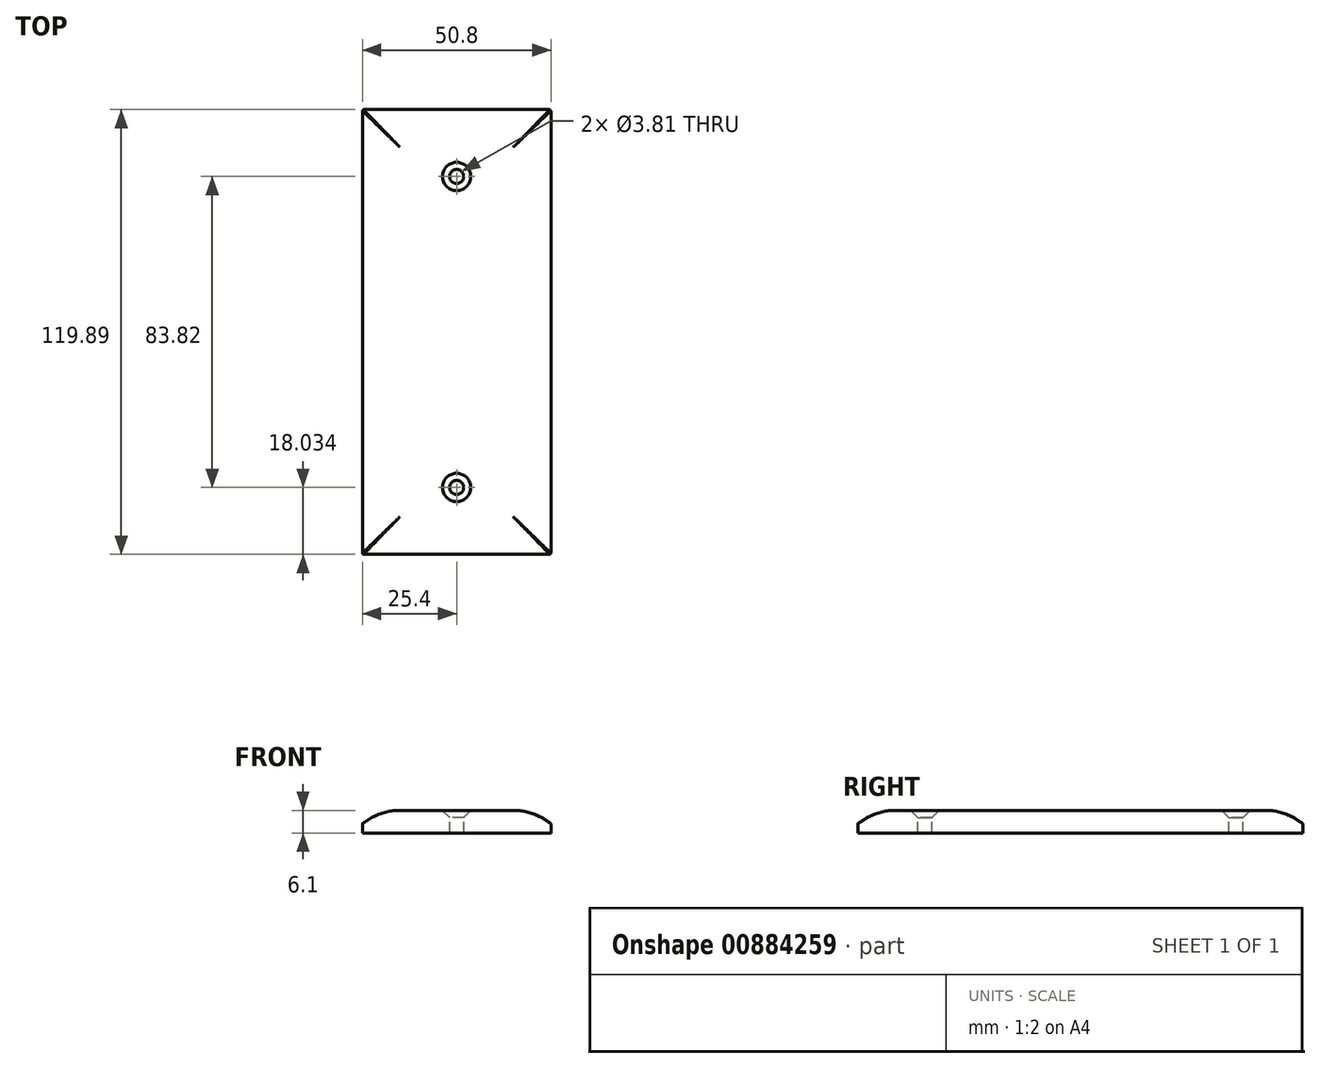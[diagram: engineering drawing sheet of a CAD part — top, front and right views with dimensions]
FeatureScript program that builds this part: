
annotation { "Feature Type Name" : "Feature", "Feature Type Description" : "" }
export const myFeature = defineFeature(function(context is Context, id is Id, definition is map)
    precondition{}
    {
        {
            var Q0;
            Q0=qCreatedBy(makeId("Top.planeOp"),FACE);
            var sketch = newSketch(context, id + "F0", { "sketchPlane" : qUnion([Q0])});
            skLineSegment(sketch, "E0.bottom", {"start": v(0, 0) * mm, "end": v(50.8, 0) * mm});
            skLineSegment(sketch, "E0.top", {"start": v(0, 119.89) * mm, "end": v(50.8, 119.89) * mm});
            skLineSegment(sketch, "E0.left", {"start": v(0, 0) * mm, "end": v(0, 119.89) * mm});
            skLineSegment(sketch, "E0.right", {"start": v(50.8, 0) * mm, "end": v(50.8, 119.89) * mm});
            skSolve(sketch);
        }
        {
            var Q0;
            Q0 = qSketchRegion(id + "F0", true);
            extrude(context, id + "F1", {"entities" : qUnion([Q0]), "depth" : 6.1 * mm, "offsetDistance" : 25.4 * mm});
        }
        {
            var Q0;
            Q0=makeQuery(id+"F1.opExtrude","CAP_FACE",FACE,{"disambiguationData":[OSD([sQuery(id+"F0.wireOp",EDGE,"E0.bottom"),sQuery(id+"F0.wireOp",EDGE,"E0.top"),sQuery(id+"F0.wireOp",EDGE,"E0.left"),sQuery(id+"F0.wireOp",EDGE,"E0.right")])],"isStart":false});
            var sketch = newSketch(context, id + "F2", { "sketchPlane" : qUnion([Q0])});
            skLineSegment(sketch, "E1", {"start": v(25.4, 0) * mm, "end": v(25.4, 119.89) * mm, "construction": true});
            skPoint(sketch, "E2", {"position": v(25.4, 18.03) * mm});
            skPoint(sketch, "E3", {"position": v(25.4, 101.85) * mm});
            skLineSegment(sketch, "E4", {"start": v(0, 59.94) * mm, "end": v(50.8, 59.94) * mm, "construction": true});
            skPoint(sketch, "E5", {"position": v(50.8, 59.94) * mm});
            skSolve(sketch);
        }
        {
            var Q0;
            Q0=sQuery(id+"F2.wireOp",VERTEX,"E3");
            var Q1;
            Q1=sQuery(id+"F2.wireOp",VERTEX,"E2");
            var Q2;
            Q2=makeQuery(id+"F1.opExtrude","SWEPT_BODY",BODY,{"disambiguationData":[OSD([sQuery(id+"F0.wireOp",EDGE,"E0.bottom"),sQuery(id+"F0.wireOp",EDGE,"E0.top"),sQuery(id+"F0.wireOp",EDGE,"E0.left"),sQuery(id+"F0.wireOp",EDGE,"E0.right")])]});
            hole(context, id + "F3", {"style" : HoleStyle.C_SINK, "endStyle" : HoleEndStyle.THROUGH, "holeDiameter" : 3.8 * mm, "cSinkDiameter" : 7.62 * mm, "cSinkAngle" : 90 * degree, "majorDiameter" : 6.35 * mm, "isTappedThrough" : true, "tappedDepth" : 12.7 * mm, "tapClearance" : 3, "locations" : qUnion([Q0, Q1]), "scope" : qUnion([Q2])});
        }
        {
            var Q0;
            Q0=makeQuery(id+"F1.opExtrude","SWEPT_FACE",FACE,{"disambiguationData":[OSD([sQuery(id+"F0.wireOp",EDGE,"E0.bottom")])]});
            var sketch = newSketch(context, id + "F4", { "sketchPlane" : qUnion([Q0])});
            skArc(sketch, "E6", {"start": v(0.2, 2.7) * mm, "mid": v(4.9, 5.22) * mm, "end": v(10.16, 6.1) * mm});
            skLineSegment(sketch, "E7", {"start": v(25.4, 0) * mm, "end": v(25.4, 6.1) * mm, "construction": true});
            skPoint(sketch, "E8.visualSharp", {"position": v(0, 2.54) * mm});
            skLineSegment(sketch, "E9", {"start": v(10.16, 6.1) * mm, "end": v(0, 6.1) * mm});
            skLineSegment(sketch, "E10", {"start": v(0, 6.1) * mm, "end": v(0, 2.54) * mm});
            skLineSegment(sketch, "E11", {"start": v(10.16, 6.1) * mm, "end": v(25.4, 6.1) * mm, "construction": true});
            skLineSegment(sketch, "E12", {"start": v(0, 2.3) * mm, "end": v(0, 0) * mm, "construction": true});
            skArc(sketch, "E13.filletArc", {"start": v(0.2, 2.7) * mm, "mid": v(0.05, 2.52) * mm, "end": v(0, 2.3) * mm});
            skLineSegment(sketch, "E14.MirrorCS", {"start": v(40.64, 6.1) * mm, "end": v(50.8, 6.1) * mm});
            skLineSegment(sketch, "E15.MirrorCS", {"start": v(50.8, 6.1) * mm, "end": v(50.8, 2.54) * mm});
            skLineSegment(sketch, "E16", {"start": v(0, 2.54) * mm, "end": v(0, 2.3) * mm});
            skLineSegment(sketch, "E17.MirrorCS", {"start": v(50.8, 2.54) * mm, "end": v(50.8, 2.3) * mm});
            skArc(sketch, "E18.MirrorCS", {"start": v(50.6, 2.7) * mm, "mid": v(50.75, 2.52) * mm, "end": v(50.8, 2.3) * mm});
            skArc(sketch, "E19.MirrorCS", {"start": v(50.6, 2.7) * mm, "mid": v(45.9, 5.22) * mm, "end": v(40.64, 6.1) * mm});
            skSolve(sketch);
        }
        {
            var Q0;
            Q0 = qSketchRegion(id + "F4", true);
            extrude(context, id + "F5", {"entities" : qUnion([Q0]), "operationType" : NewBodyOperationType.REMOVE, "endBound" : BoundingType.THROUGH_ALL, "oppositeDirection" : true, "depth" : 25.4 * mm, "offsetDistance" : 25.4 * mm});
        }
        {
            var Q0;
            Q0=makeQuery(id+"F1.opExtrude","SWEPT_FACE",FACE,{"disambiguationData":[OSD([sQuery(id+"F0.wireOp",EDGE,"E0.left")])]});
            var sketch = newSketch(context, id + "F6", { "sketchPlane" : qUnion([Q0])});
            skLineSegment(sketch, "E20", {"start": v(-119.89, 6.1) * mm, "end": v(-119.89, 2.54) * mm});
            skLineSegment(sketch, "E21", {"start": v(-119.89, 6.1) * mm, "end": v(-109.73, 6.1) * mm});
            skLineSegment(sketch, "E22", {"start": v(-59.94, 0) * mm, "end": v(-59.94, 6.1) * mm, "construction": true});
            skLineSegment(sketch, "E23", {"start": v(-109.73, 6.1) * mm, "end": v(-59.94, 6.1) * mm, "construction": true});
            skLineSegment(sketch, "E24", {"start": v(-119.89, 2.3) * mm, "end": v(-119.89, 0) * mm, "construction": true});
            skArc(sketch, "E25", {"start": v(-109.73, 6.1) * mm, "mid": v(-115, 5.22) * mm, "end": v(-119.7, 2.7) * mm});
            skPoint(sketch, "E26.visualSharp", {"position": v(-119.89, 2.54) * mm});
            skArc(sketch, "E26.filletArc", {"start": v(-119.7, 2.7) * mm, "mid": v(-119.84, 2.52) * mm, "end": v(-119.89, 2.3) * mm});
            skLineSegment(sketch, "E27.MirrorCS", {"start": v(0, 6.1) * mm, "end": v(0, 2.54) * mm});
            skLineSegment(sketch, "E28", {"start": v(-119.89, 2.54) * mm, "end": v(-119.89, 2.3) * mm});
            skLineSegment(sketch, "E29.MirrorCS", {"start": v(0, 2.54) * mm, "end": v(0, 2.3) * mm});
            skLineSegment(sketch, "E30.MirrorCS", {"start": v(0, 6.1) * mm, "end": v(-10.16, 6.1) * mm});
            skArc(sketch, "E31.MirrorCS", {"start": v(-10.16, 6.1) * mm, "mid": v(-4.9, 5.22) * mm, "end": v(-0.2, 2.7) * mm});
            skArc(sketch, "E32.MirrorCS", {"start": v(-0.2, 2.7) * mm, "mid": v(-0.05, 2.52) * mm, "end": v(0, 2.3) * mm});
            skSolve(sketch);
        }
        {
            var Q0;
            Q0 = qSketchRegion(id + "F6", true);
            extrude(context, id + "F7", {"entities" : qUnion([Q0]), "operationType" : NewBodyOperationType.REMOVE, "endBound" : BoundingType.THROUGH_ALL, "oppositeDirection" : true, "depth" : 25.4 * mm, "offsetDistance" : 25.4 * mm});
        }
        {
            var Q0;
            Q0=makeQuery(id+"F1.opExtrude","SWEPT_EDGE",EDGE,{"disambiguationData":[OSD([sQuery(id+"F0.wireOp",EDGE,"E0.top"),sQuery(id+"F0.wireOp",EDGE,"E0.left")])]});
            var Q1;
            Q1=makeQuery(id+"F7.boolean.opBoolean","INTERSECT",EDGE,{"derivedFrom":[makeQuery(id+"F5.boolean.opBoolean","COPY",FACE,{"derivedFrom":makeQuery(id+"F5.opExtrude","SWEPT_FACE",FACE,{"disambiguationData":[OSD([sQuery(id+"F4.wireOp",EDGE,"E13.filletArc")])]})}),makeQuery(id+"F7.opExtrude","SWEPT_FACE",FACE,{"disambiguationData":[OSD([sQuery(id+"F6.wireOp",EDGE,"E26.filletArc")])]})]});
            var Q2;
            Q2=makeQuery(id+"F7.boolean.opBoolean","INTERSECT",EDGE,{"derivedFrom":[makeQuery(id+"F5.boolean.opBoolean","COPY",FACE,{"derivedFrom":makeQuery(id+"F5.opExtrude","SWEPT_FACE",FACE,{"disambiguationData":[OSD([sQuery(id+"F4.wireOp",EDGE,"E6")])]})}),makeQuery(id+"F7.opExtrude","SWEPT_FACE",FACE,{"disambiguationData":[OSD([sQuery(id+"F6.wireOp",EDGE,"E25")])]})]});
            var Q3;
            Q3=makeQuery(id+"F1.opExtrude","SWEPT_EDGE",EDGE,{"disambiguationData":[OSD([sQuery(id+"F0.wireOp",EDGE,"E0.top"),sQuery(id+"F0.wireOp",EDGE,"E0.right")])]});
            var Q4;
            Q4=makeQuery(id+"F7.boolean.opBoolean","INTERSECT",EDGE,{"derivedFrom":[makeQuery(id+"F5.boolean.opBoolean","COPY",FACE,{"derivedFrom":makeQuery(id+"F5.opExtrude","SWEPT_FACE",FACE,{"disambiguationData":[OSD([sQuery(id+"F4.wireOp",EDGE,"E18.MirrorCS")])]})}),makeQuery(id+"F7.opExtrude","SWEPT_FACE",FACE,{"disambiguationData":[OSD([sQuery(id+"F6.wireOp",EDGE,"E26.filletArc")])]})]});
            var Q5;
            Q5=makeQuery(id+"F7.boolean.opBoolean","INTERSECT",EDGE,{"derivedFrom":[makeQuery(id+"F5.boolean.opBoolean","COPY",FACE,{"derivedFrom":makeQuery(id+"F5.opExtrude","SWEPT_FACE",FACE,{"disambiguationData":[OSD([sQuery(id+"F4.wireOp",EDGE,"E19.MirrorCS")])]})}),makeQuery(id+"F7.opExtrude","SWEPT_FACE",FACE,{"disambiguationData":[OSD([sQuery(id+"F6.wireOp",EDGE,"E25")])]})]});
            var Q6;
            Q6=makeQuery(id+"F1.opExtrude","SWEPT_EDGE",EDGE,{"disambiguationData":[OSD([sQuery(id+"F0.wireOp",EDGE,"E0.bottom"),sQuery(id+"F0.wireOp",EDGE,"E0.right")])]});
            var Q7;
            Q7=makeQuery(id+"F7.boolean.opBoolean","INTERSECT",EDGE,{"derivedFrom":[makeQuery(id+"F5.boolean.opBoolean","COPY",FACE,{"derivedFrom":makeQuery(id+"F5.opExtrude","SWEPT_FACE",FACE,{"disambiguationData":[OSD([sQuery(id+"F4.wireOp",EDGE,"E18.MirrorCS")])]})}),makeQuery(id+"F7.opExtrude","SWEPT_FACE",FACE,{"disambiguationData":[OSD([sQuery(id+"F6.wireOp",EDGE,"E32.MirrorCS")])]})]});
            var Q8;
            Q8=makeQuery(id+"F7.boolean.opBoolean","INTERSECT",EDGE,{"derivedFrom":[makeQuery(id+"F5.boolean.opBoolean","COPY",FACE,{"derivedFrom":makeQuery(id+"F5.opExtrude","SWEPT_FACE",FACE,{"disambiguationData":[OSD([sQuery(id+"F4.wireOp",EDGE,"E19.MirrorCS")])]})}),makeQuery(id+"F7.opExtrude","SWEPT_FACE",FACE,{"disambiguationData":[OSD([sQuery(id+"F6.wireOp",EDGE,"E31.MirrorCS")])]})]});
            var Q9;
            Q9=makeQuery(id+"F1.opExtrude","SWEPT_EDGE",EDGE,{"disambiguationData":[OSD([sQuery(id+"F0.wireOp",EDGE,"E0.bottom"),sQuery(id+"F0.wireOp",EDGE,"E0.left")])]});
            var Q10;
            Q10=makeQuery(id+"F7.boolean.opBoolean","INTERSECT",EDGE,{"derivedFrom":[makeQuery(id+"F5.boolean.opBoolean","COPY",FACE,{"derivedFrom":makeQuery(id+"F5.opExtrude","SWEPT_FACE",FACE,{"disambiguationData":[OSD([sQuery(id+"F4.wireOp",EDGE,"E13.filletArc")])]})}),makeQuery(id+"F7.opExtrude","SWEPT_FACE",FACE,{"disambiguationData":[OSD([sQuery(id+"F6.wireOp",EDGE,"E32.MirrorCS")])]})]});
            var Q11;
            Q11=makeQuery(id+"F7.boolean.opBoolean","INTERSECT",EDGE,{"derivedFrom":[makeQuery(id+"F5.boolean.opBoolean","COPY",FACE,{"derivedFrom":makeQuery(id+"F5.opExtrude","SWEPT_FACE",FACE,{"disambiguationData":[OSD([sQuery(id+"F4.wireOp",EDGE,"E6")])]})}),makeQuery(id+"F7.opExtrude","SWEPT_FACE",FACE,{"disambiguationData":[OSD([sQuery(id+"F6.wireOp",EDGE,"E31.MirrorCS")])]})]});
            fillet(context, id + "F8", {"entities" : qUnion([Q0, Q1, Q2, Q3, Q4, Q5, Q6, Q7, Q8, Q9, Q10, Q11]), "radius" : 0.5 * mm, "tangentPropagation" : true, "allowEdgeOverflow" : false});
        }
    });
